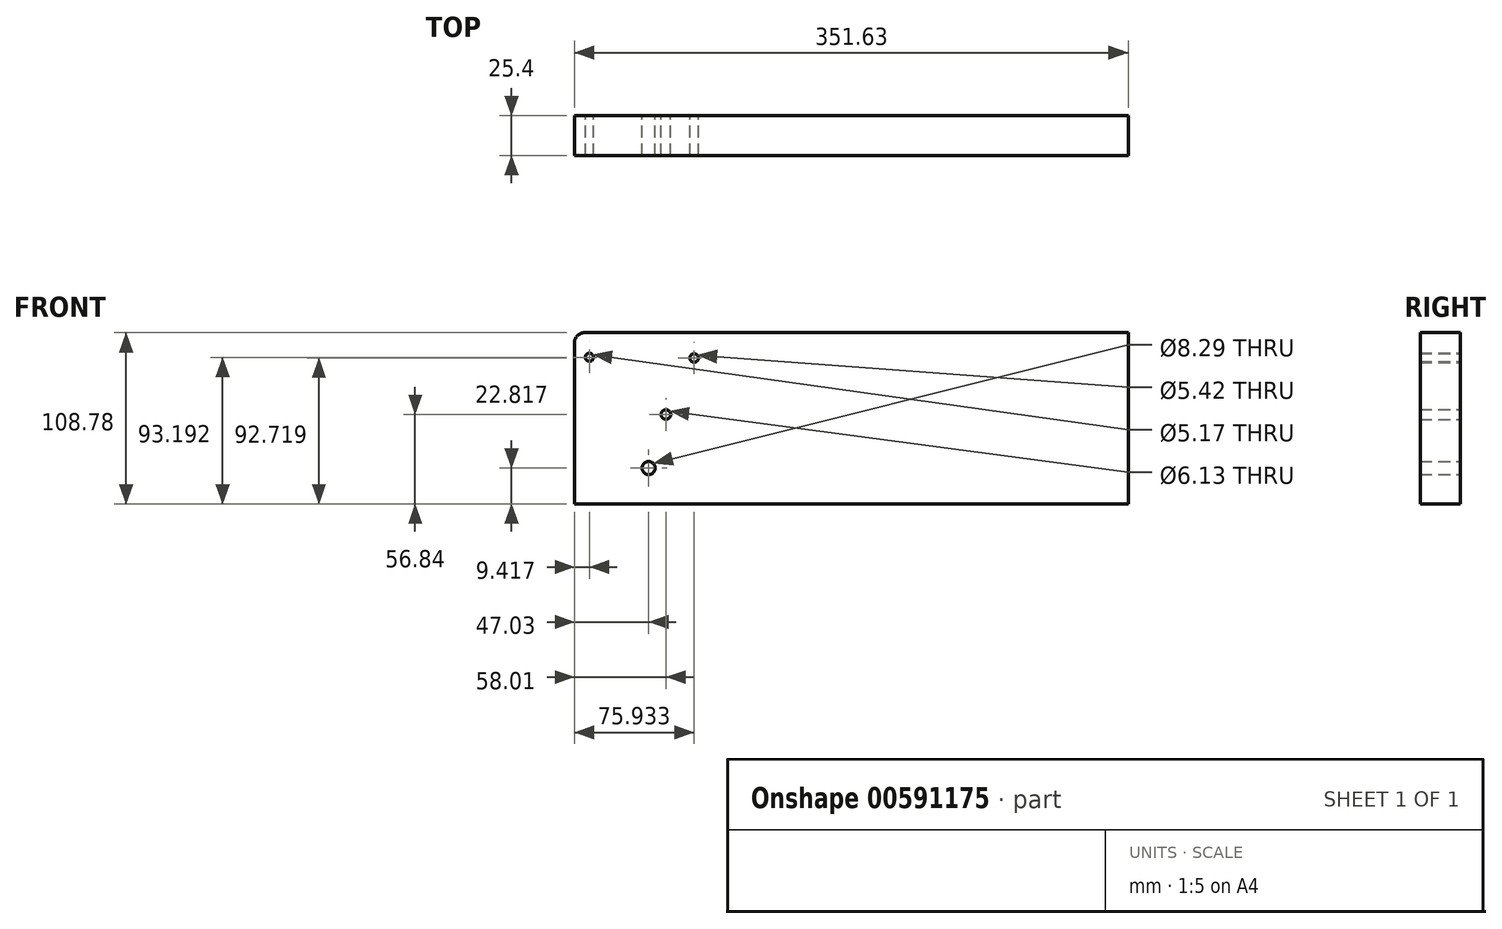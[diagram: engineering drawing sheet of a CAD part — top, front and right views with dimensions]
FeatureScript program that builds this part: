
annotation { "Feature Type Name" : "Feature", "Feature Type Description" : "" }
export const myFeature = defineFeature(function(context is Context, id is Id, definition is map)
    precondition{}
    {
        {
            var Q0;
            Q0=qCreatedBy(makeId("Front.planeOp"),FACE);
            var sketch = newSketch(context, id + "F0", { "sketchPlane" : qUnion([Q0])});
            skLineSegment(sketch, "E0.bottom", {"start": v(-40.68, 51.94) * mm, "end": v(50.6, 51.94) * mm});
            skLineSegment(sketch, "E0.top", {"start": v(-47.03, -56.84) * mm, "end": v(50.6, -56.84) * mm});
            skLineSegment(sketch, "E0.left", {"start": v(-47.03, 45.59) * mm, "end": v(-47.03, -56.84) * mm});
            skLineSegment(sketch, "E0.right", {"start": v(50.6, 51.94) * mm, "end": v(50.6, -56.84) * mm});
            skCircle(sketch, "E1", {"center": v(-37.61, 36.35) * mm, "radius": 2.59 * mm});
            skCircle(sketch, "E2", {"center": v(28.9, 35.88) * mm, "radius": 2.71 * mm});
            skCircle(sketch, "E3", {"center": v(0, -34.02) * mm, "radius": 4.15 * mm});
            skCircle(sketch, "E4", {"center": v(10.98, 0) * mm, "radius": 3.06 * mm});
            skPoint(sketch, "E5.visualSharp", {"position": v(-47.03, 51.94) * mm});
            skArc(sketch, "E5.filletArc", {"start": v(-40.68, 51.94) * mm, "mid": v(-45.17, 50.08) * mm, "end": v(-47.03, 45.59) * mm});
            skSolve(sketch);
        }
        {
            var Q0;
            Q0=makeQuery(id+"F0.imprint","IMPRINT",FACE,{"disambiguationData":[TD([[makeQuery(id+"F0.imprint","IMPRINT",EDGE,{"derivedFrom":sQuery(id+"F0.wireOp",EDGE,"E0.bottom")}),-1.0]])]});
            extrude(context, id + "F1", {"entities" : qUnion([Q0]), "depth" : 25.4 * mm, "offsetDistance" : 25.4 * mm});
        }
        {
            var Q0;
            Q0=makeQuery(id+"F1.opExtrude","SWEPT_FACE",FACE,{"disambiguationData":[OSD([sQuery(id+"F0.wireOp",EDGE,"E0.right")])]});
            extrude(context, id + "F2", {"entities" : qUnion([Q0]), "operationType" : NewBodyOperationType.ADD, "depth" : 254 * mm, "offsetDistance" : 25.4 * mm});
        }
        {
            var Q0;
            Q0=qCreatedBy(makeId("Front.planeOp"),FACE);
            var sketch = newSketch(context, id + "F3", { "sketchPlane" : qUnion([Q0])});
            skCircle(sketch, "E6", {"center": v(-16.5, 25.41) * mm, "radius": 11.35 * mm});
            skSolve(sketch);
        }
        {
            var Q0;
            Q0=sQuery(id+"F3.wireOp",EDGE,"E6");
            extrude(context, id + "F4", {"bodyType" : ToolBodyType.SURFACE, "surfaceEntities" : qUnion([Q0]), "depth" : 254 * mm, "offsetDistance" : 25.4 * mm, "hasSecondDirection" : true, "secondDirectionOppositeDirection" : true, "secondDirectionDepth" : 254 * mm});
        }
    });
